# Revit family: FU_Table_Sandler_Cono 4001 - Complete
name_source: partatom
category: Furniture
units: mm (PartAtom-declared; Revit-internal decimal feet)

## family parameters
Always vertical = Yes
Cut with Voids When Loaded = No
OmniClass Number = 23.40.20.00
OmniClass Title = General Furniture and Specialties
Render Appearance Source = Family Geometry
Room Calculation Point = No
Shared = No
Work Plane-Based = No

## types (3) — shared parameters
Depth = 450 mm  [stored 1.47638 ft]
Height = 720 mm  [stored 2.3622 ft]
Manufacturer = Sandler
URL = https://www.sandlerseating.com
Width = 450 mm  [stored 1.47638 ft]
zero-valued in all types: Default Elevation

## per-type parameters (varying)
| type | Description | Model | Top Type |
| Cono 4001 - D32 | Dining table with metal base. 80cm/32"-diameter table top in a woodgrain or lacquered finish, with a reverse knife edge profile. 75cm/29.5" high. Other top profiles/materials available by special request. | Cono 4001 D32 | FU_Top_Sandler_EF125 : 125EF Top 80dia |
| Cono 4001 - D36 | Dining table with metal base. 90cm/36"-diameter table top in a woodgrain or lacquered finish, with a reverse knife edge profile. 75cm/29.5" high. Other top profiles/materials available by special request. | Cono 4001 D36 | FU_Top_Sandler_EF125 : 125EF Top 90dia |
| Cono 4001 - D40 | Dining table with metal base. 100cm/40"-diameter table top in a woodgrain or lacquered finish, with a reverse knife edge profile. 75cm/29.5" high. Other top profiles/materials available by special request. | Cono 4001 D40 | FU_Top_Sandler_EF125 : 125EF Top 100dia |

note: [stored X ft] marks values corroborated as IEEE doubles in the binary element streams (Revit-internal decimal feet)

## geometry (parser evidence)
native form markers: Sweep x6
no freeform markers — native parametric forms only
